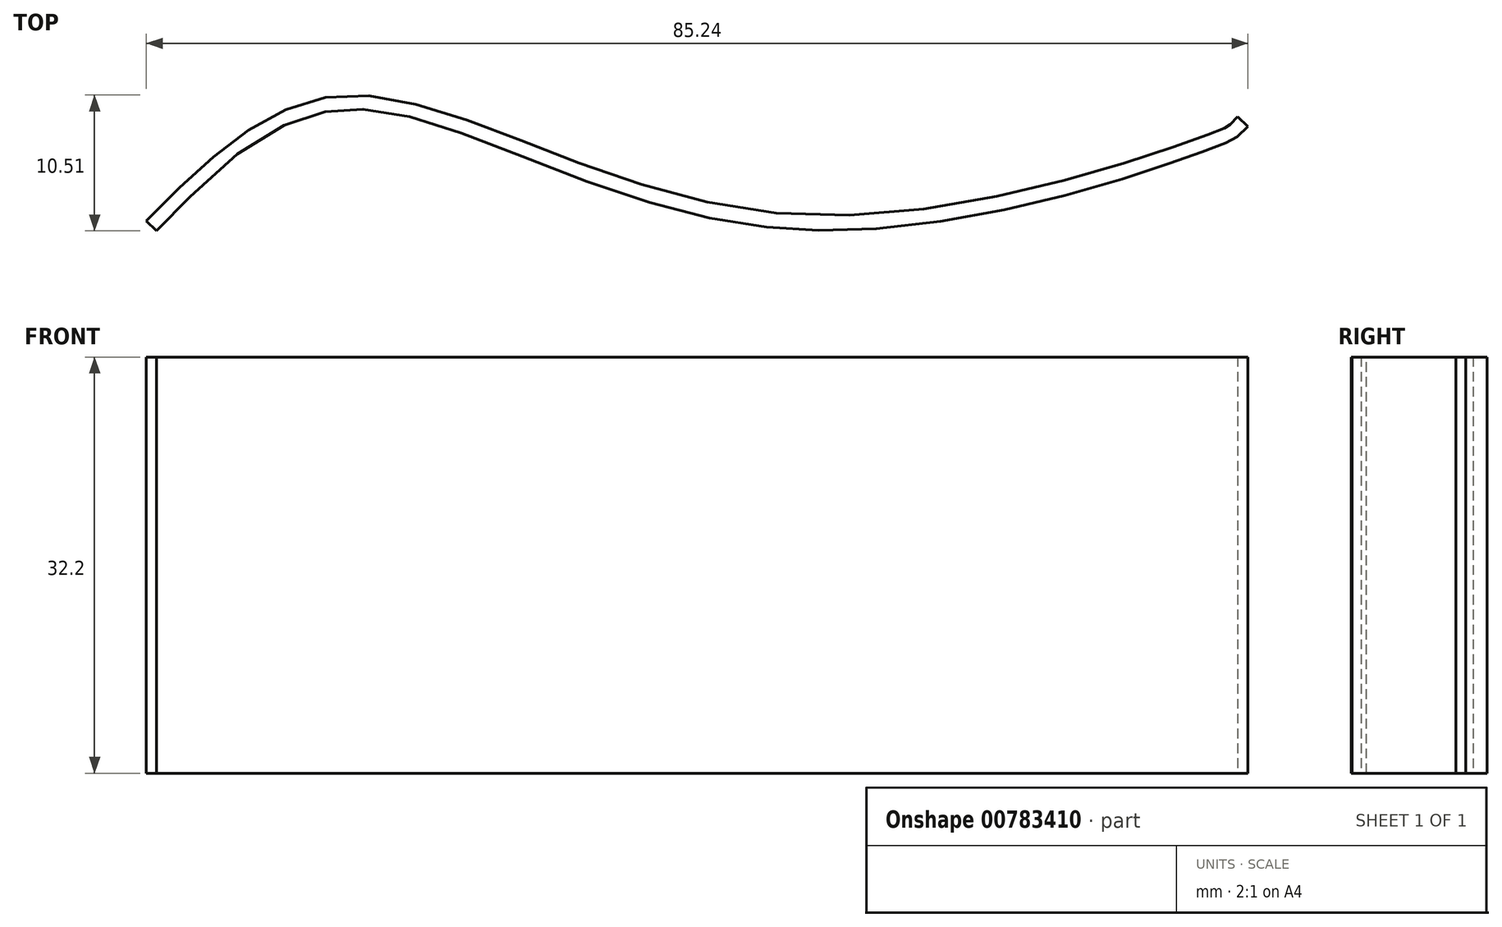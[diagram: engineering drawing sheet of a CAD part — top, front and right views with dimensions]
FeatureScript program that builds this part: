
annotation { "Feature Type Name" : "Feature", "Feature Type Description" : "" }
export const myFeature = defineFeature(function(context is Context, id is Id, definition is map)
    precondition{}
    {
        {
            var Q0;
            Q0=qCreatedBy(makeId("Top.planeOp"),FACE);
            var sketch = newSketch(context, id + "F0", { "sketchPlane" : qUnion([Q0])});
            skFitSpline(sketch, "E0", {"points": [v(-55.62, -2.25) * mm, v(-39.97, 7.47) * mm, v(-5.34, -1.78) * mm, v(27.63, 4.86) * mm, v(28.1, 5.1) * mm, v(28.82, 5.81) * mm], "startDerivative": vector(58.8, 59.39) * mm, "endDerivative": vector(14.54, 15.25) * mm});
            skFitSpline(sketch, "E1.0", {"points": [v(-54.84, -3.03) * mm, v(-53.62, -1.79) * mm, v(-51.19, 0.66) * mm, v(-48.1, 3.27) * mm, v(-45.53, 4.85) * mm, v(-43.55, 5.74) * mm, v(-41.83, 6.2) * mm, v(-40.4, 6.37) * mm, v(-38.94, 6.4) * mm, v(-36.96, 6.18) * mm, v(-34.38, 5.57) * mm, v(-31.62, 4.68) * mm, v(-27.68, 3.2) * mm, v(-23.4, 1.49) * mm, v(-18.77, -0.15) * mm, v(-15.14, -1.26) * mm, v(-11.33, -2.17) * mm, v(-8.02, -2.68) * mm, v(-5.28, -2.9) * mm, v(-2.5, -2.98) * mm, v(1.02, -2.85) * mm, v(5.25, -2.38) * mm, v(9.38, -1.68) * mm, v(13.32, -0.81) * mm, v(17, 0.15) * mm, v(20.33, 1.13) * mm, v(22.72, 1.91) * mm, v(24.37, 2.48) * mm, v(25.46, 2.87) * mm, v(26.4, 3.21) * mm, v(27.16, 3.5) * mm, v(27.65, 3.69) * mm, v(27.94, 3.8) * mm, v(28.1, 3.87) * mm, v(28.24, 3.92) * mm, v(28.38, 3.98) * mm, v(28.55, 4.06) * mm, v(28.72, 4.18) * mm, v(28.84, 4.28) * mm, v(28.98, 4.4) * mm, v(29.16, 4.58) * mm, v(29.39, 4.81) * mm, v(29.54, 4.97) * mm, v(29.62, 5.05) * mm]});
            skLineSegment(sketch, "E2", {"start": v(-55.62, -2.25) * mm, "end": v(-54.84, -3.03) * mm});
            skLineSegment(sketch, "E3", {"start": v(28.82, 5.81) * mm, "end": v(29.62, 5.05) * mm});
            skSolve(sketch);
        }
        {
            var Q0;
            Q0=makeQuery(id+"F0.imprint","IMPRINT",FACE,{"disambiguationData":[TD([[makeQuery(id+"F0.imprint","IMPRINT",EDGE,{"derivedFrom":sQuery(id+"F0.wireOp",EDGE,"E0")}),-1.0]])]});
            extrude(context, id + "F1", {"entities" : qUnion([Q0]), "depth" : 32.2 * mm, "offsetDistance" : 25 * mm});
        }
    });
